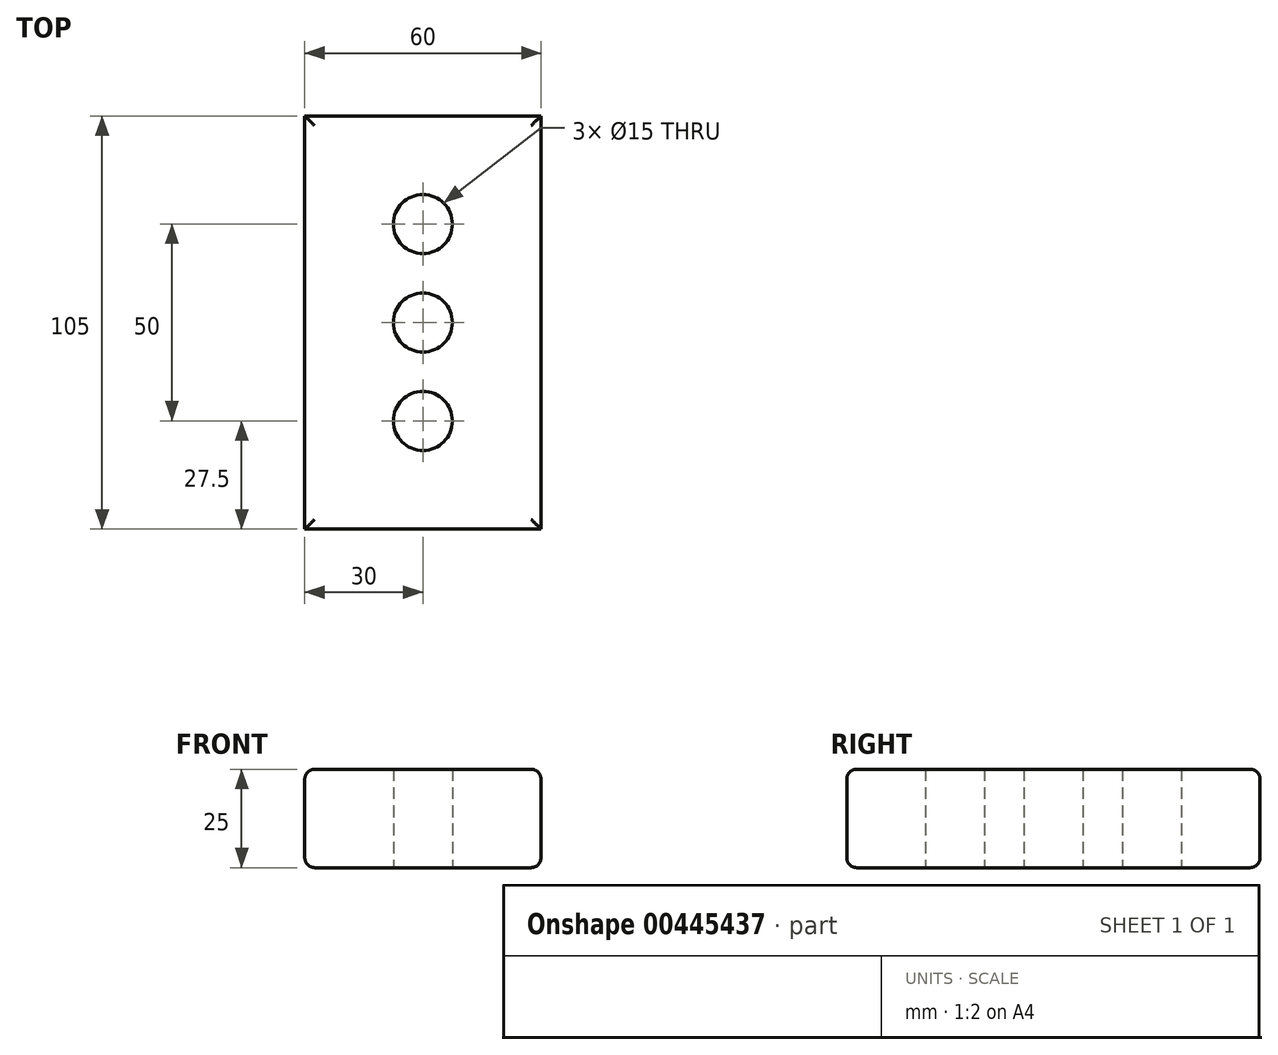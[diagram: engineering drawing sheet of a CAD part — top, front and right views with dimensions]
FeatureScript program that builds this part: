
annotation { "Feature Type Name" : "Feature", "Feature Type Description" : "" }
export const myFeature = defineFeature(function(context is Context, id is Id, definition is map)
    precondition{}
    {
        {
            var Q0;
            Q0=qCreatedBy(makeId("Top.planeOp"),FACE);
            var sketch = newSketch(context, id + "F0", { "sketchPlane" : qUnion([Q0])});
            skLineSegment(sketch, "E0.bottom", {"start": v(-30, 52.5) * mm, "end": v(30, 52.5) * mm});
            skLineSegment(sketch, "E0.top", {"start": v(-30, -52.5) * mm, "end": v(30, -52.5) * mm});
            skLineSegment(sketch, "E0.left", {"start": v(-30, 52.5) * mm, "end": v(-30, -52.5) * mm});
            skLineSegment(sketch, "E0.right", {"start": v(30, 52.5) * mm, "end": v(30, -52.5) * mm});
            skPoint(sketch, "E0.middle", {"position": v(0, 0) * mm});
            skCircle(sketch, "E1", {"center": v(0, 0) * mm, "radius": 7.5 * mm});
            skCircle(sketch, "E2", {"center": v(0, 25) * mm, "radius": 7.5 * mm});
            skCircle(sketch, "E3", {"center": v(0, -25) * mm, "radius": 7.5 * mm});
            skSolve(sketch);
        }
        {
            var Q0;
            Q0 = qSketchRegion(id + "F0", true);
            var Q1;
            Q1=makeQuery(id+"F0.imprint","IMPRINT",FACE,{"disambiguationData":[TD([[makeQuery(id+"F0.imprint","IMPRINT",EDGE,{"derivedFrom":sQuery(id+"F0.wireOp",EDGE,"E0.bottom")}),-1.0]])]});
            extrude(context, id + "F1", {"entities" : qUnion([Q0, Q1]), "depth" : 20 * mm});
        }
        {
            var Q0;
            Q0 = qSketchRegion(id + "F0", true);
            extrude(context, id + "F2", {"entities" : qUnion([Q0]), "operationType" : NewBodyOperationType.ADD, "depth" : 25 * mm});
        }
        {
            var Q0;
            Q0=makeQuery(id+"F2.opExtrude","CAP_EDGE",EDGE,{"disambiguationData":[OSD([sQuery(id+"F0.wireOp",EDGE,"E0.left")])],"isStart":false});
            var Q1;
            Q1=makeQuery(id+"F2.opExtrude","CAP_EDGE",EDGE,{"disambiguationData":[OSD([sQuery(id+"F0.wireOp",EDGE,"E0.bottom")])],"isStart":false});
            var Q2;
            Q2=makeQuery(id+"F2.opExtrude","CAP_EDGE",EDGE,{"disambiguationData":[OSD([sQuery(id+"F0.wireOp",EDGE,"E0.right")])],"isStart":false});
            var Q3;
            Q3=makeQuery(id+"F2.opExtrude","CAP_EDGE",EDGE,{"disambiguationData":[OSD([sQuery(id+"F0.wireOp",EDGE,"E0.top")])],"isStart":false});
            var Q4;
            Q4=makeQuery(id+"F1.opExtrude","CAP_EDGE",EDGE,{"disambiguationData":[OSD([sQuery(id+"F0.wireOp",EDGE,"E0.left")])],"isStart":true});
            var Q5;
            Q5=makeQuery(id+"F1.opExtrude","CAP_EDGE",EDGE,{"disambiguationData":[OSD([sQuery(id+"F0.wireOp",EDGE,"E0.bottom")])],"isStart":true});
            var Q6;
            Q6=makeQuery(id+"F1.opExtrude","CAP_EDGE",EDGE,{"disambiguationData":[OSD([sQuery(id+"F0.wireOp",EDGE,"E0.right")])],"isStart":true});
            var Q7;
            Q7=makeQuery(id+"F1.opExtrude","CAP_EDGE",EDGE,{"disambiguationData":[OSD([sQuery(id+"F0.wireOp",EDGE,"E0.top")])],"isStart":true});
            fillet(context, id + "F3", {"entities" : qUnion([Q0, Q1, Q2, Q3, Q4, Q5, Q6, Q7]), "radius" : 2.5 * mm, "tangentPropagation" : true, "allowEdgeOverflow" : false});
        }
    });
